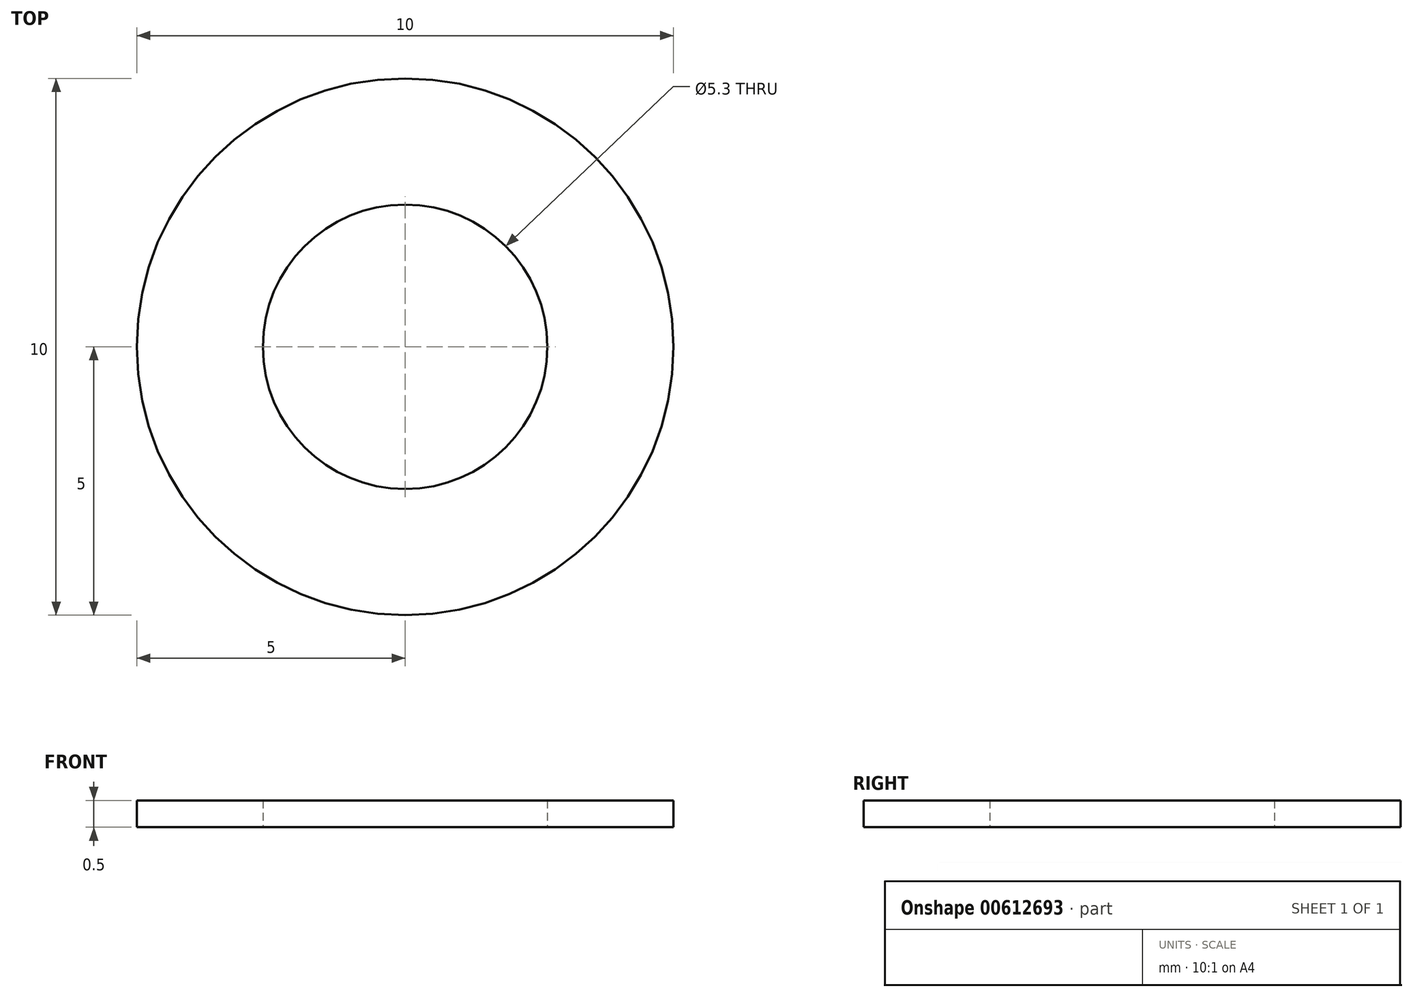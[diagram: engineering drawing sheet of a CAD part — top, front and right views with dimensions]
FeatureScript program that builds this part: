
annotation { "Feature Type Name" : "Feature", "Feature Type Description" : "" }
export const myFeature = defineFeature(function(context is Context, id is Id, definition is map)
    precondition{}
    {
        {
            var Q0;
            Q0=qCreatedBy(makeId("Top.planeOp"),FACE);
            var sketch = newSketch(context, id + "F0", { "sketchPlane" : qUnion([Q0])});
            skCircle(sketch, "E0", {"center": v(0, 0) * mm, "radius": 2.65 * mm});
            skCircle(sketch, "E1", {"center": v(0, 0) * mm, "radius": 5 * mm});
            skSolve(sketch);
        }
        {
            var Q0;
            Q0=makeQuery(id+"F0.imprint","IMPRINT",FACE,{"disambiguationData":[TD([[makeQuery(id+"F0.imprint","IMPRINT",EDGE,{"derivedFrom":sQuery(id+"F0.wireOp",EDGE,"E0")}),-1.0]])]});
            extrude(context, id + "F1", {"entities" : qUnion([Q0]), "depth" : 0.5 * mm, "offsetDistance" : 25 * mm});
        }
    });
